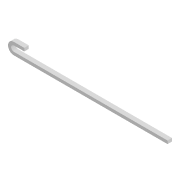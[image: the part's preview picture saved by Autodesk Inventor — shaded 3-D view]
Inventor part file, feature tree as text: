
AUTODESK INVENTOR PART (.ipt)
format: ipt  version: 2020 (Build 240168000, 168)  size: 84,480 bytes
history: native  units: mm
features: extrude x1, sketch x1
ambient origin geometry x8: Origin, YZ Plane, XZ Plane, XY Plane, X Axis, Y Axis, Z Axis, Center Point
bodies: Solid1 (feature_tree)
feature tree (2):
  extrude  "Extrusion1"  Depth=20.0mm
  sketch  "Sketch1"  dims[d0=76.0mm d1=20.0mm d2=20.0mm d4=1000.0mm d5=29.0mm d6=0.0mm d7=68.0mm]
